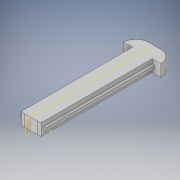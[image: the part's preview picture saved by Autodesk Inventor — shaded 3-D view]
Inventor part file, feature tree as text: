
AUTODESK INVENTOR PART (.ipt)
format: ipt  version: 2018 (Build 220112000, 112)  size: 167,936 bytes
history: native  units: in
note: dims shown in document units (in); Inventor stores cm internally (conversion verified against a paired STEP export)
features: sketch x6, extrude x5, mirror x3, plane x1, fillet x1
ambient origin geometry x8: Origin, YZ Plane, XZ Plane, XY Plane, X Axis, Y Axis, Z Axis, Center Point
bodies: Solid1 (feature_tree)
feature tree (16):
  extrude  "Extrusion1"  Depth=2.25in
  sketch  "Sketch2"  dims[d2=0.24in d3=0.0in d4=0.06in]
  extrude  "Extrusion2"  Depth=0.06in
  plane  "Work Plane1"
  mirror  "Mirror1"
  extrude  "Extrusion3"  Depth=0.09in
  fillet  "Fillet2"  Radius=0.0525in
  extrude  "Extrusion4"  Depth=0.24in
  mirror  "Mirror2"
  extrude  "Extrusion5"  Depth=0.375in
  mirror  "Mirror3"
  sketch  "Sketch1"  dims[d0=0.4in d1=2.25in]
  sketch  "Sketch3"  dims[d5=2.25in d6=0.09in d7=0.0525in d8=0.0in]
  sketch  "Sketch4"  dims[d9=0.25in d10=0.0in d12=0.24in]
  sketch  "Sketch5"  dims[d13=0.75in d14=0.375in]
  sketch  "Sketch6"  dims[d15=0.25in d16=0.25in d17=0.3in d18=0.0in d19=2.2in d20=0.3in d21=0.0in]
